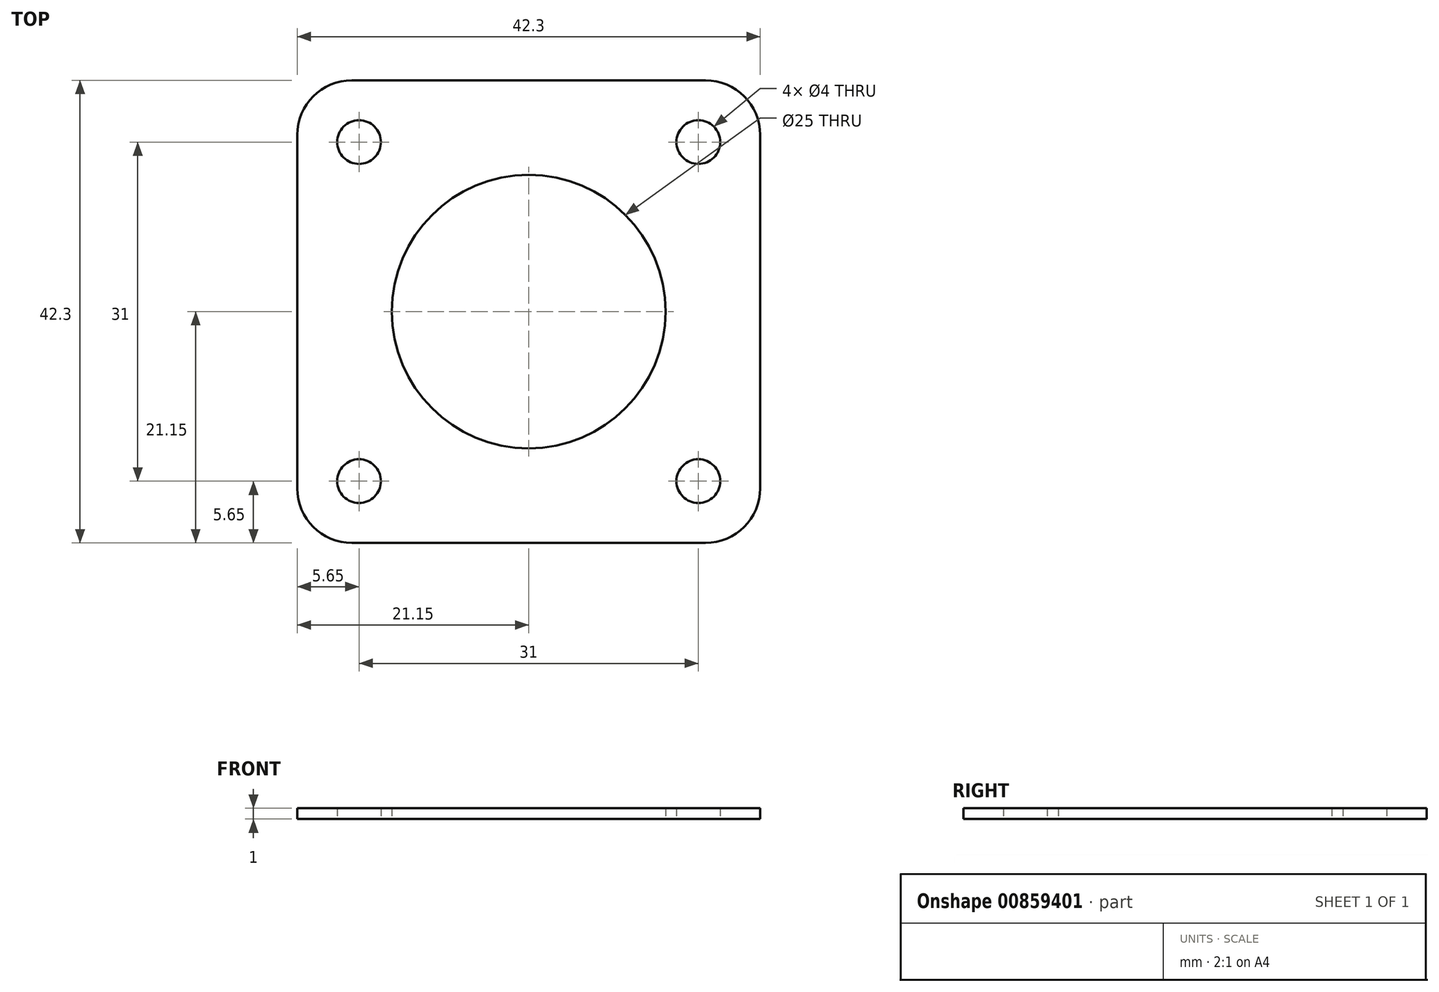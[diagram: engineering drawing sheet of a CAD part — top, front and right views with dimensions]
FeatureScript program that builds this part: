
annotation { "Feature Type Name" : "Feature", "Feature Type Description" : "" }
export const myFeature = defineFeature(function(context is Context, id is Id, definition is map)
    precondition{}
    {
        {
            var Q0;
            Q0=qCreatedBy(makeId("Top.planeOp"),FACE);
            var sketch = newSketch(context, id + "F0", { "sketchPlane" : qUnion([Q0])});
            skLineSegment(sketch, "E0.bottom", {"start": v(16.15, 21.15) * mm, "end": v(-16.15, 21.15) * mm});
            skLineSegment(sketch, "E0.top", {"start": v(16.15, -21.15) * mm, "end": v(-16.15, -21.15) * mm});
            skLineSegment(sketch, "E0.left", {"start": v(21.15, 16.15) * mm, "end": v(21.15, -16.15) * mm});
            skLineSegment(sketch, "E0.right", {"start": v(-21.15, 16.15) * mm, "end": v(-21.15, -16.15) * mm});
            skPoint(sketch, "E0.middle", {"position": v(0, 0) * mm});
            skLineSegment(sketch, "E1.bottom", {"start": v(15.5, 15.5) * mm, "end": v(-15.5, 15.5) * mm, "construction": true});
            skLineSegment(sketch, "E1.top", {"start": v(15.5, -15.5) * mm, "end": v(-15.5, -15.5) * mm, "construction": true});
            skLineSegment(sketch, "E1.left", {"start": v(15.5, 15.5) * mm, "end": v(15.5, -15.5) * mm, "construction": true});
            skLineSegment(sketch, "E1.right", {"start": v(-15.5, 15.5) * mm, "end": v(-15.5, -15.5) * mm, "construction": true});
            skCircle(sketch, "E2", {"center": v(-15.5, 15.5) * mm, "radius": 2 * mm});
            skCircle(sketch, "E3", {"center": v(15.5, 15.5) * mm, "radius": 2 * mm});
            skCircle(sketch, "E4", {"center": v(-15.5, -15.5) * mm, "radius": 2 * mm});
            skCircle(sketch, "E5", {"center": v(15.5, -15.5) * mm, "radius": 2 * mm});
            skCircle(sketch, "E6", {"center": v(0, 0) * mm, "radius": 12.5 * mm});
            skPoint(sketch, "E7.visualSharp", {"position": v(-21.15, 21.15) * mm});
            skArc(sketch, "E7.filletArc", {"start": v(-16.15, 21.15) * mm, "mid": v(-19.69, 19.69) * mm, "end": v(-21.15, 16.15) * mm});
            skPoint(sketch, "E8.visualSharp", {"position": v(21.15, 21.15) * mm});
            skArc(sketch, "E8.filletArc", {"start": v(21.15, 16.15) * mm, "mid": v(19.69, 19.69) * mm, "end": v(16.15, 21.15) * mm});
            skPoint(sketch, "E9.visualSharp", {"position": v(21.15, -21.15) * mm});
            skArc(sketch, "E9.filletArc", {"start": v(16.15, -21.15) * mm, "mid": v(19.69, -19.69) * mm, "end": v(21.15, -16.15) * mm});
            skPoint(sketch, "E10.visualSharp", {"position": v(-21.15, -21.15) * mm});
            skArc(sketch, "E10.filletArc", {"start": v(-21.15, -16.15) * mm, "mid": v(-19.69, -19.69) * mm, "end": v(-16.15, -21.15) * mm});
            skSolve(sketch);
        }
        {
            var Q0;
            Q0=makeQuery(id+"F0.imprint","IMPRINT",FACE,{"disambiguationData":[TD([[makeQuery(id+"F0.imprint","IMPRINT",EDGE,{"derivedFrom":sQuery(id+"F0.wireOp",EDGE,"E0.bottom")}),1.0]])]});
            extrude(context, id + "F1", {"entities" : qUnion([Q0]), "depth" : 1 * mm, "offsetDistance" : 25 * mm});
        }
    });
